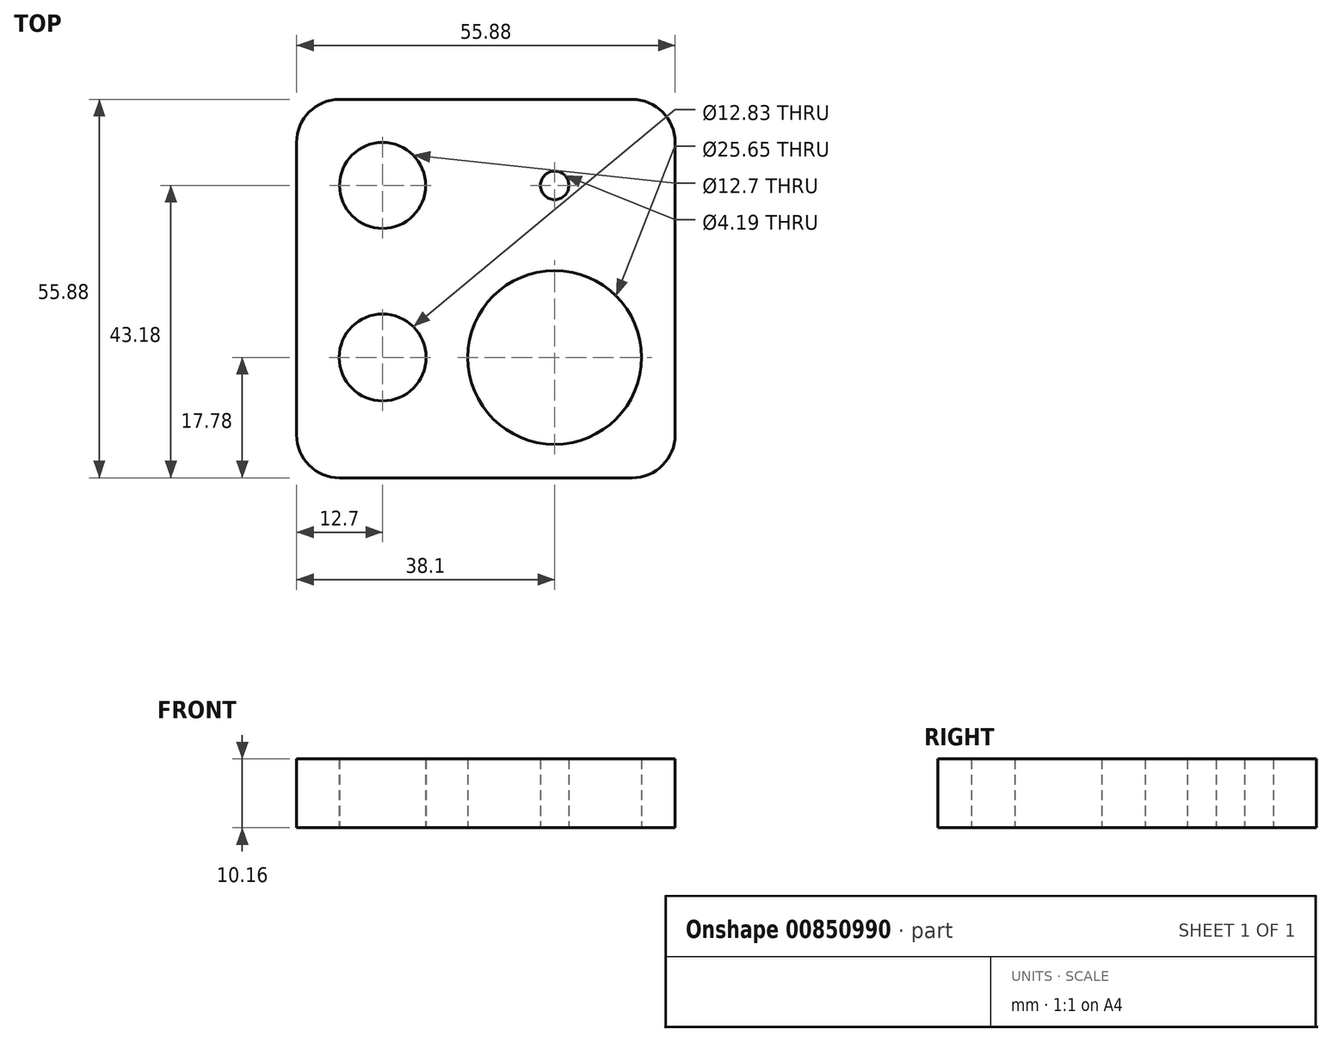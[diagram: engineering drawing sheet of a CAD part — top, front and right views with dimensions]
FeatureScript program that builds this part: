
annotation { "Feature Type Name" : "Feature", "Feature Type Description" : "" }
export const myFeature = defineFeature(function(context is Context, id is Id, definition is map)
    precondition{}
    {
        {
            var Q0;
            Q0=qCreatedBy(makeId("Top.planeOp"),FACE);
            var sketch = newSketch(context, id + "F0", { "sketchPlane" : qUnion([Q0])});
            skCircle(sketch, "E0", {"center": v(0, 0) * mm, "radius": 6.41 * mm});
            skCircle(sketch, "E1", {"center": v(25.4, 0) * mm, "radius": 12.83 * mm});
            skCircle(sketch, "E2", {"center": v(0, 25.4) * mm, "radius": 6.35 * mm});
            skCircle(sketch, "E3", {"center": v(25.4, 25.4) * mm, "radius": 2.1 * mm});
            skLineSegment(sketch, "E4", {"start": v(25.4, 0) * mm, "end": v(25.4, 25.4) * mm, "construction": true});
            skLineSegment(sketch, "E5", {"start": v(25.4, 0) * mm, "end": v(0, 0) * mm, "construction": true});
            skLineSegment(sketch, "E6", {"start": v(0, 0) * mm, "end": v(0, 25.4) * mm, "construction": true});
            skLineSegment(sketch, "E7", {"start": v(0, 25.4) * mm, "end": v(25.4, 25.4) * mm, "construction": true});
            skLineSegment(sketch, "E8.bottom", {"start": v(-6.35, 38.1) * mm, "end": v(36.83, 38.1) * mm});
            skLineSegment(sketch, "E8.top", {"start": v(-6.35, -17.78) * mm, "end": v(36.83, -17.78) * mm});
            skLineSegment(sketch, "E8.left", {"start": v(-12.7, 31.75) * mm, "end": v(-12.7, -11.43) * mm});
            skLineSegment(sketch, "E8.right", {"start": v(43.18, 31.75) * mm, "end": v(43.18, -11.43) * mm});
            skPoint(sketch, "E9.visualSharp", {"position": v(-12.7, 38.1) * mm});
            skArc(sketch, "E9.filletArc", {"start": v(-6.35, 38.1) * mm, "mid": v(-10.84, 36.24) * mm, "end": v(-12.7, 31.75) * mm});
            skPoint(sketch, "E10.visualSharp", {"position": v(43.18, 38.1) * mm});
            skArc(sketch, "E10.filletArc", {"start": v(43.18, 31.75) * mm, "mid": v(41.32, 36.24) * mm, "end": v(36.83, 38.1) * mm});
            skPoint(sketch, "E11.visualSharp", {"position": v(43.18, -17.78) * mm});
            skArc(sketch, "E11.filletArc", {"start": v(36.83, -17.78) * mm, "mid": v(41.32, -15.92) * mm, "end": v(43.18, -11.43) * mm});
            skPoint(sketch, "E12.visualSharp", {"position": v(-12.7, -17.78) * mm});
            skArc(sketch, "E12.filletArc", {"start": v(-12.7, -11.43) * mm, "mid": v(-10.84, -15.92) * mm, "end": v(-6.35, -17.78) * mm});
            skSolve(sketch);
        }
        {
            var Q0;
            Q0=makeQuery(id+"F0.imprint","IMPRINT",FACE,{"disambiguationData":[TD([[makeQuery(id+"F0.imprint","IMPRINT",EDGE,{"derivedFrom":sQuery(id+"F0.wireOp",EDGE,"E0")}),-1.0]])]});
            extrude(context, id + "F1", {"entities" : qUnion([Q0]), "depth" : 10.16 * mm, "offsetDistance" : 25.4 * mm});
        }
    });
